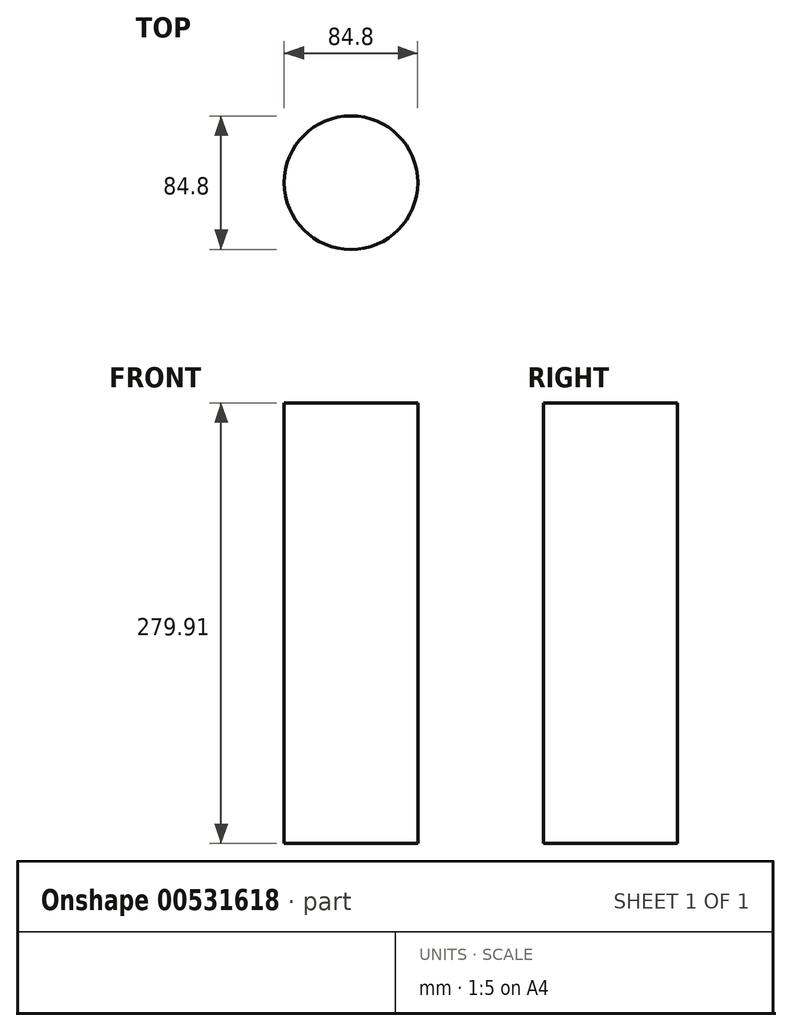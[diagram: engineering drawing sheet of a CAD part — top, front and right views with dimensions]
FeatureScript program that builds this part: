
annotation { "Feature Type Name" : "Feature", "Feature Type Description" : "" }
export const myFeature = defineFeature(function(context is Context, id is Id, definition is map)
    precondition{}
    {
        {
            var Q0;
            Q0=qCreatedBy(makeId("Top.planeOp"),FACE);
            var sketch = newSketch(context, id + "F0", { "sketchPlane" : qUnion([Q0])});
            skCircle(sketch, "E0", {"center": v(0, 0) * mm, "radius": 2.36 * mm});
            skCircle(sketch, "E1", {"center": v(0, 0) * mm, "radius": 32.72 * mm});
            skSolve(sketch);
        }
        {
            var Q0;
            Q0 = qSketchRegion(id + "F0", true);
            extrude(context, id + "F1", {"entities" : qUnion([Q0]), "depth" : 25.4 * mm, "offsetDistance" : 25.4 * mm});
        }
        {
            var Q0;
            Q0=makeQuery(id+"F1.opExtrude","CAP_FACE",FACE,{"disambiguationData":[OSD([sQuery(id+"F0.wireOp",EDGE,"E0"),sQuery(id+"F0.wireOp",EDGE,"E1")])],"isStart":false});
            extrude(context, id + "F2", {"entities" : qUnion([Q0]), "operationType" : NewBodyOperationType.ADD, "depth" : 64 * mm, "offsetDistance" : 25.4 * mm});
        }
        {
            var Q0;
            Q0=makeQuery(id+"F2.opExtrude","CAP_FACE",FACE,{"disambiguationData":[OSD([sQuery(id+"F0.wireOp",EDGE,"E0"),sQuery(id+"F0.wireOp",EDGE,"E1")])],"isStart":false});
            shell(context, id + "F3", {"entities" : qUnion([Q0]), "thickness" : 2.54 * mm});
        }
        {
            var Q0;
            Q0=makeQuery(id+"F1.opExtrude","SWEPT_BODY",BODY,{"disambiguationData":[OSD([sQuery(id+"F0.wireOp",EDGE,"E0"),sQuery(id+"F0.wireOp",EDGE,"E1")])]});
            deleteBodies(context, id + "F4", {"entities" : qUnion([Q0])});
        }
        {
            var Q0;
            Q0=qCreatedBy(makeId("Top.planeOp"),FACE);
            var sketch = newSketch(context, id + "F5", { "sketchPlane" : qUnion([Q0])});
            skCircle(sketch, "E2", {"center": v(0, 0) * mm, "radius": 42.4 * mm});
            skSolve(sketch);
        }
        {
            var Q0;
            Q0 = qSketchRegion(id + "F5", true);
            extrude(context, id + "F6", {"entities" : qUnion([Q0]), "depth" : 25.4 * mm, "offsetDistance" : 25.4 * mm});
        }
        {
            var Q0;
            Q0=makeQuery(id+"F6.opExtrude","CAP_FACE",FACE,{"disambiguationData":[OSD([sQuery(id+"F5.wireOp",EDGE,"E2")])],"isStart":false});
            extrude(context, id + "F7", {"entities" : qUnion([Q0]), "operationType" : NewBodyOperationType.ADD, "depth" : 77.72 * mm, "offsetDistance" : 25.4 * mm});
        }
        {
            var Q0;
            Q0=makeQuery(id+"F7.opExtrude","CAP_FACE",FACE,{"disambiguationData":[OSD([sQuery(id+"F5.wireOp",EDGE,"E2")])],"isStart":false});
            var sketch = newSketch(context, id + "F8", { "sketchPlane" : qUnion([Q0])});
            skSolve(sketch);
        }
        {
            var Q0;
            Q0=makeQuery(id+"F8.imprint","IMPRINT",FACE,{"disambiguationData":[TD([[makeQuery(id+"F8.imprint","IMPRINT",EDGE,{"derivedFrom":makeQuery(id+"F7.opExtrude","CAP_EDGE",EDGE,{"disambiguationData":[OSD([sQuery(id+"F5.wireOp",EDGE,"E2")])],"isStart":false})}),1.0]])]});
            var Q1;
            Q1=makeQuery(id+"F7.opExtrude","CAP_FACE",FACE,{"disambiguationData":[OSD([sQuery(id+"F5.wireOp",EDGE,"E2")])],"isStart":false});
            var Q2;
            Q2=makeQuery(id+"F6.opExtrude","CAP_FACE",FACE,{"disambiguationData":[OSD([sQuery(id+"F5.wireOp",EDGE,"E2")])],"isStart":true});
            extrude(context, id + "F9", {"entities" : qUnion([Q0, Q1, Q2]), "operationType" : NewBodyOperationType.ADD, "depth" : 127 * mm, "offsetDistance" : 25.4 * mm});
        }
        {
            var Q0;
            Q0=qCreatedBy(makeId("Top.planeOp"),FACE);
            var sketch = newSketch(context, id + "F10", { "sketchPlane" : qUnion([Q0])});
            skCircle(sketch, "E3", {"center": v(0, 0) * mm, "radius": 37.9 * mm});
            skSolve(sketch);
        }
        {
            var Q0;
            Q0 = qSketchRegion(id + "F10", true);
            extrude(context, id + "F11", {"entities" : qUnion([Q0]), "operationType" : NewBodyOperationType.ADD, "depth" : 173.23 * mm, "offsetDistance" : 25.4 * mm});
        }
        {
            var Q0;
            Q0=makeQuery(id+"F6.opExtrude","CAP_FACE",FACE,{"disambiguationData":[OSD([sQuery(id+"F5.wireOp",EDGE,"E2")])],"isStart":true});
            extrude(context, id + "F12", {"entities" : qUnion([Q0]), "operationType" : NewBodyOperationType.ADD, "oppositeDirection" : true, "depth" : 279.9 * mm, "offsetDistance" : 25.4 * mm});
        }
    });
